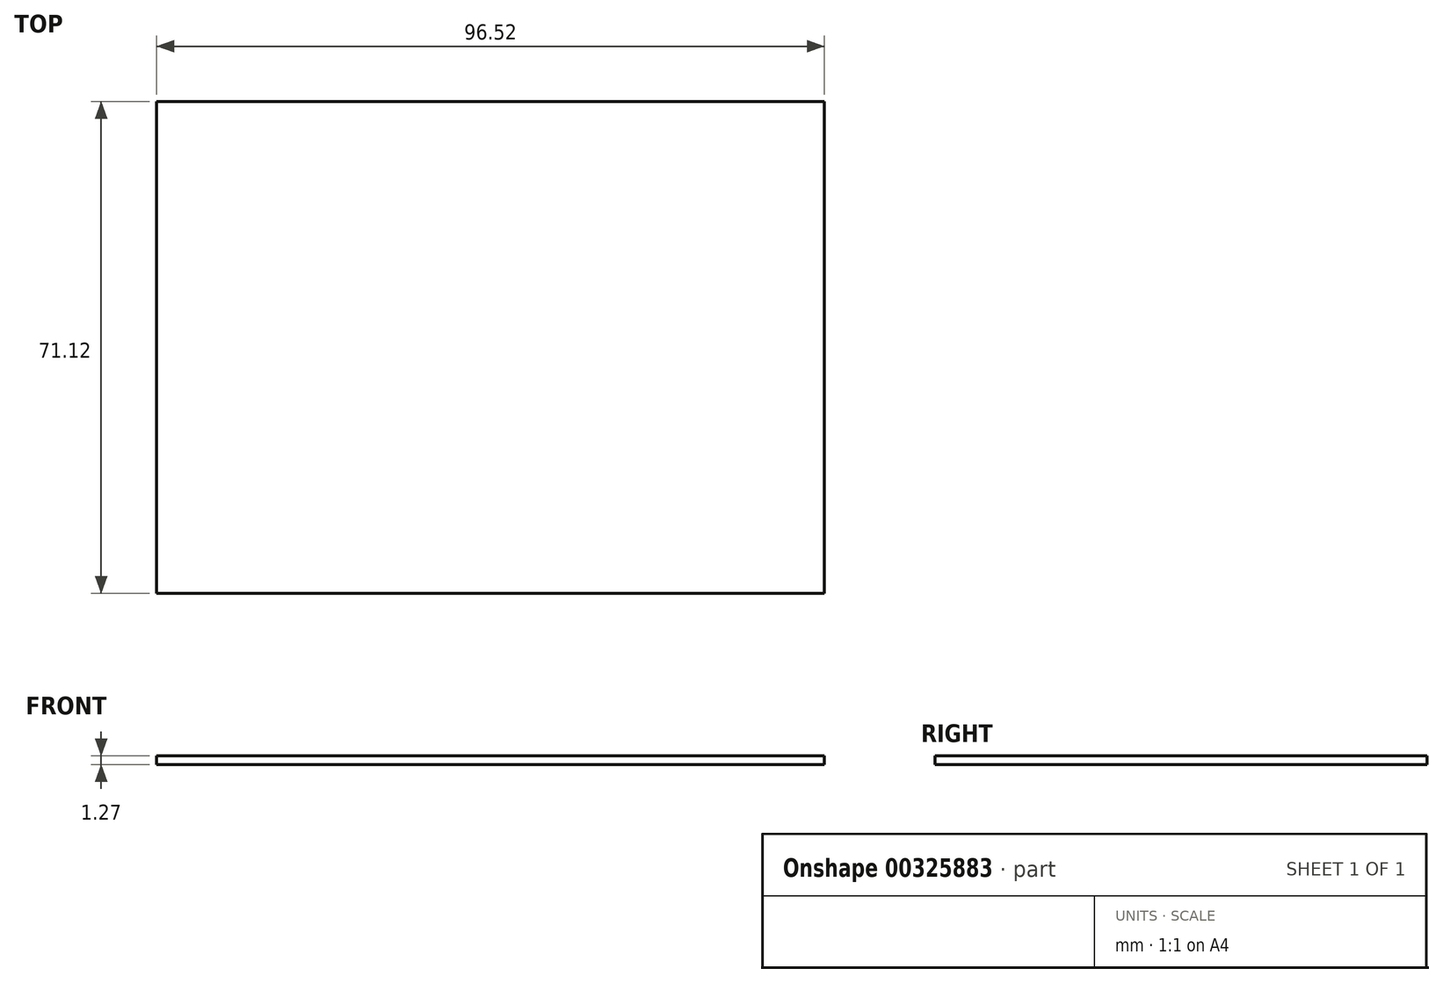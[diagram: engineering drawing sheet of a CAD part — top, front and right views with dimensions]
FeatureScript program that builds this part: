
annotation { "Feature Type Name" : "Feature", "Feature Type Description" : "" }
export const myFeature = defineFeature(function(context is Context, id is Id, definition is map)
    precondition{}
    {
        {
            var Q0;
            Q0=qCreatedBy(makeId("Top.planeOp"),FACE);
            var sketch = newSketch(context, id + "F0", { "sketchPlane" : qUnion([Q0])});
            skLineSegment(sketch, "E0.bottom", {"start": v(-48.26, 35.56) * mm, "end": v(48.26, 35.56) * mm});
            skLineSegment(sketch, "E0.top", {"start": v(-48.26, -35.56) * mm, "end": v(48.26, -35.56) * mm});
            skLineSegment(sketch, "E0.left", {"start": v(-48.26, 35.56) * mm, "end": v(-48.26, -35.56) * mm});
            skLineSegment(sketch, "E0.right", {"start": v(48.26, 35.56) * mm, "end": v(48.26, -35.56) * mm});
            skPoint(sketch, "E0.middle", {"position": v(0, 0) * mm});
            skSolve(sketch);
        }
        {
            var Q0;
            Q0=makeQuery(id+"F0.imprint","IMPRINT",FACE,{"disambiguationData":[TD([[makeQuery(id+"F0.imprint","IMPRINT",EDGE,{"derivedFrom":sQuery(id+"F0.wireOp",EDGE,"E0.bottom")}),-1.0]])]});
            extrude(context, id + "F1", {"entities" : qUnion([Q0]), "depth" : 1.27 * mm});
        }
    });
